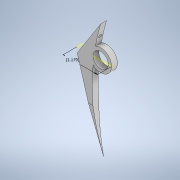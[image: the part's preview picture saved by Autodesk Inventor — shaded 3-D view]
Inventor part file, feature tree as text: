
AUTODESK INVENTOR PART (.ipt)
format: ipt  version: 2022 (Build 260153000, 153)  size: 132,608 bytes
history: native  units: in
note: dims shown in document units (in); Inventor stores cm internally (conversion verified against a paired STEP export)
features: sketch x4, extrude x3
ambient origin geometry x8: Origin, YZ Plane, XZ Plane, XY Plane, X Axis, Y Axis, Z Axis, Center Point
bodies: Solid1 (feature_tree)
feature tree (7):
  extrude  "Extrusion1"  Depth=0.75in
  extrude  "Extrusion2"  Depth=0.5909in
  extrude  "Extrusion3"  Depth=1.0125in TaperAngle=0.0deg
  sketch  "Sketch4"  dims[d8=0.1in d9=1.0125in d10=0.0in d11=1.1787in]
  sketch  "Sketch1"  dims[d0=0.52in d1=0.75in]
  sketch  "Sketch2"  dims[d2=0.2in d3=0.0in d4=0.5909in]
  sketch  "Sketch3"  dims[d5=0.5909in d6=1.0125in d7=0.0in]
